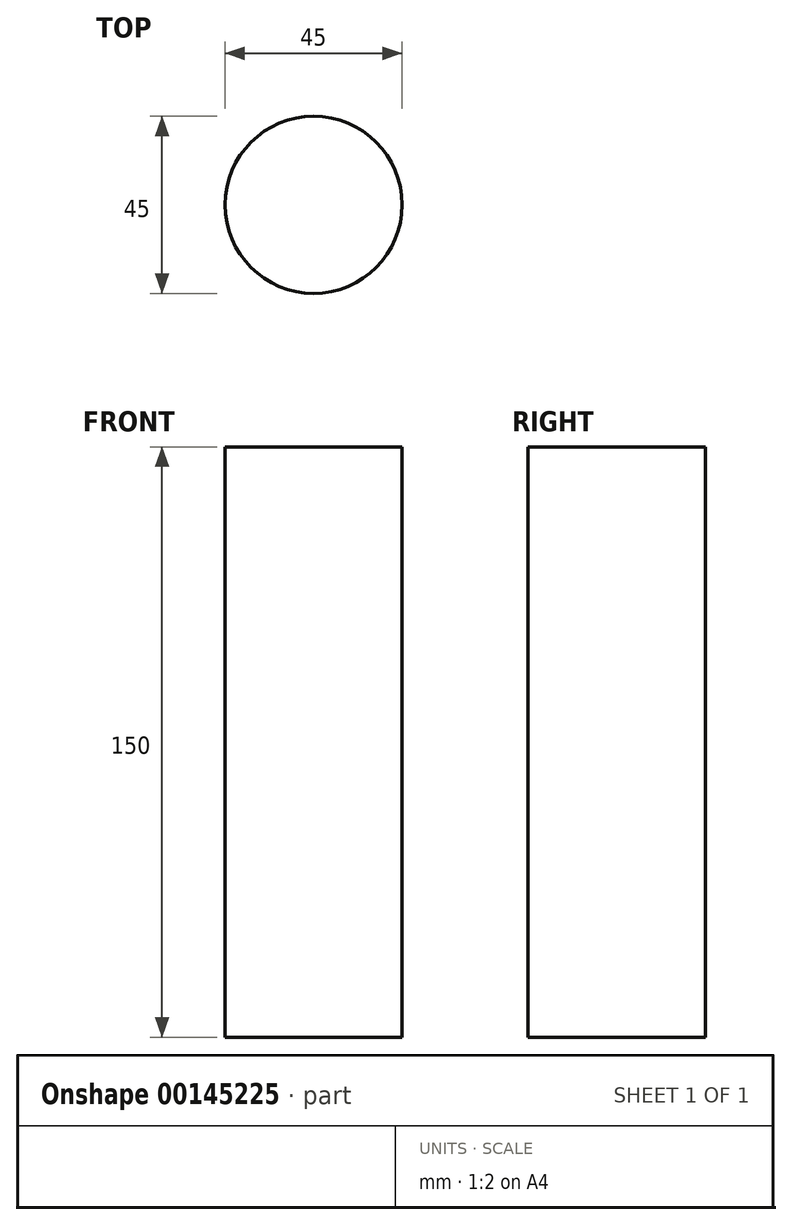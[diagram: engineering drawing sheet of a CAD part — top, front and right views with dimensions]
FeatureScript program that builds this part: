
annotation { "Feature Type Name" : "Feature", "Feature Type Description" : "" }
export const myFeature = defineFeature(function(context is Context, id is Id, definition is map)
    precondition{}
    {
        {
            var Q0;
            Q0=qCreatedBy(makeId("Top.planeOp"),FACE);
            var sketch = newSketch(context, id + "F0", { "sketchPlane" : qUnion([Q0])});
            skCircle(sketch, "E0", {"center": v(0, 0) * mm, "radius": 22.5 * mm});
            skSolve(sketch);
        }
        {
            var Q0;
            Q0 = qSketchRegion(id + "F0", true);
            extrude(context, id + "F1", {"entities" : qUnion([Q0]), "depth" : 150 * mm});
        }
    });
